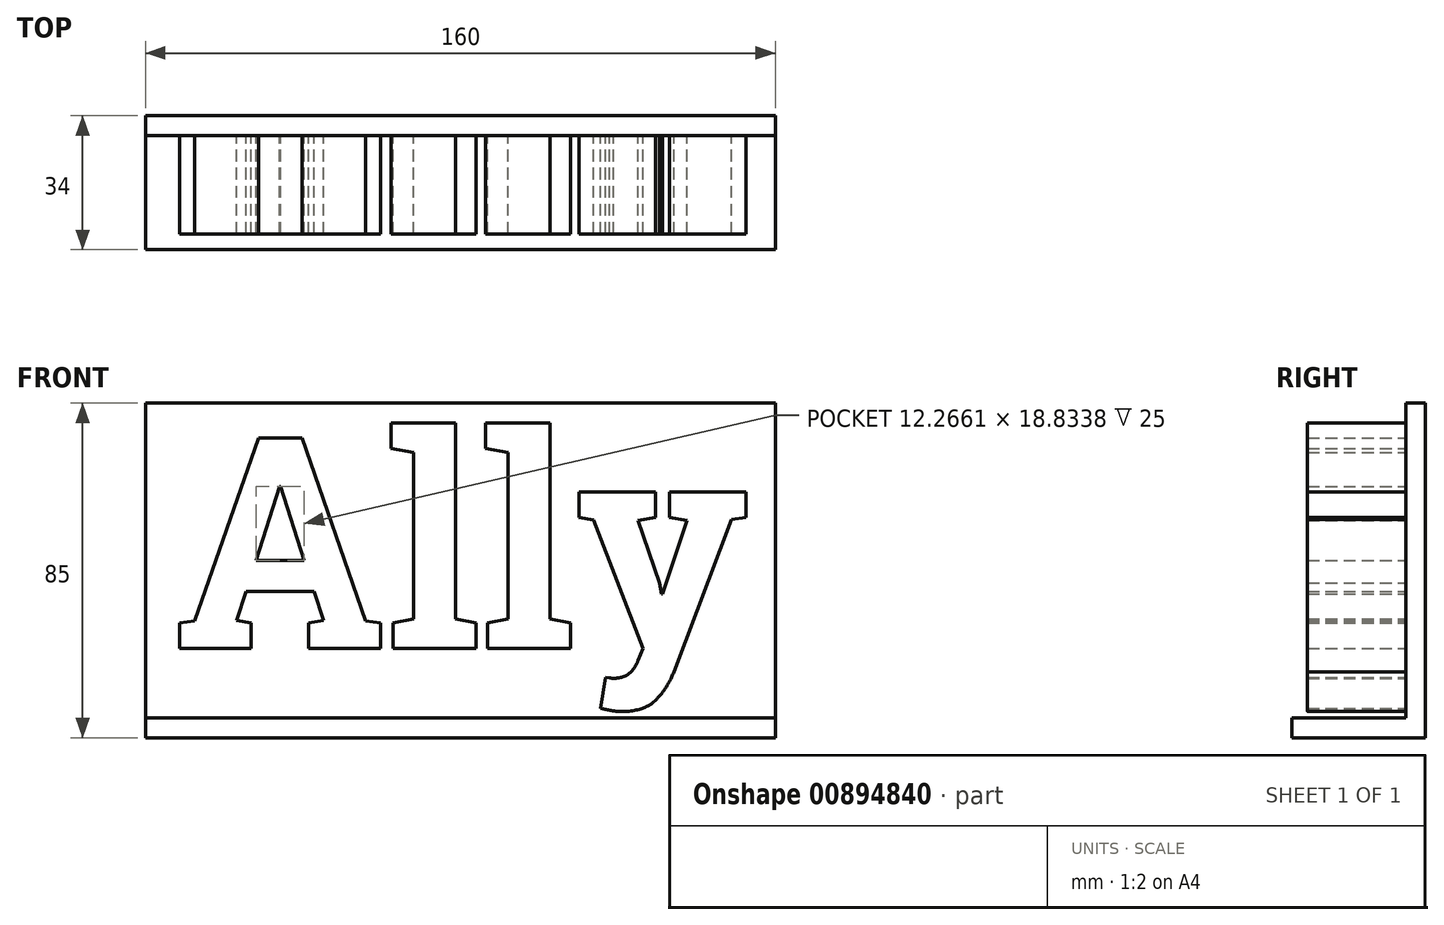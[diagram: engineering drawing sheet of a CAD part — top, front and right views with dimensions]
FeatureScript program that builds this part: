
annotation { "Feature Type Name" : "Feature", "Feature Type Description" : "" }
export const myFeature = defineFeature(function(context is Context, id is Id, definition is map)
    precondition{}
    {
        {
            var Q0;
            Q0=qCreatedBy(makeId("Front.planeOp"),FACE);
            var sketch = newSketch(context, id + "F0", { "sketchPlane" : qUnion([Q0])});
            skText(sketch, "E0", { "text": "Ally", "fontName": "RobotoSlab-Bold.ttf"});
            const initialGuessF0  = {"E0": [-0.06363, 0.04586, 1, 0, 0.05414]};
            skSetInitialGuess(sketch, initialGuessF0);
            skSolve(sketch);
        }
        {
            var Q0;
            Q0 = qSketchRegion(id + "F0", true);
            extrude(context, id + "F1", {"entities" : qUnion([Q0]), "depth" : 25 * mm, "offsetDistance" : 25 * mm});
        }
        {
            var Q0;
            Q0=qCreatedBy(makeId("Front.planeOp"),FACE);
            var sketch = newSketch(context, id + "F2", { "sketchPlane" : qUnion([Q0])});
            skLineSegment(sketch, "E1.bottom", {"start": v(-70.78, 108.16) * mm, "end": v(89.22, 108.16) * mm});
            skLineSegment(sketch, "E1.top", {"start": v(-70.78, 28.16) * mm, "end": v(89.22, 28.16) * mm});
            skLineSegment(sketch, "E1.left", {"start": v(-70.78, 108.16) * mm, "end": v(-70.78, 28.16) * mm});
            skLineSegment(sketch, "E1.right", {"start": v(89.22, 108.16) * mm, "end": v(89.22, 28.16) * mm});
            skSolve(sketch);
        }
        {
            var Q0;
            Q0=makeQuery(id+"F2.imprint","IMPRINT",FACE,{"disambiguationData":[TD([[makeQuery(id+"F2.imprint","IMPRINT",EDGE,{"derivedFrom":sQuery(id+"F2.wireOp",EDGE,"E1.bottom")}),-1.0]])]});
            extrude(context, id + "F3", {"entities" : qUnion([Q0]), "operationType" : NewBodyOperationType.ADD, "oppositeDirection" : true, "depth" : 5 * mm, "offsetDistance" : 25 * mm});
        }
        {
            var Q0;
            Q0=makeQuery(id+"F3.opExtrude","CAP_FACE",FACE,{"disambiguationData":[OSD([sQuery(id+"F2.wireOp",EDGE,"E1.bottom"),sQuery(id+"F2.wireOp",EDGE,"E1.top"),sQuery(id+"F2.wireOp",EDGE,"E1.left"),sQuery(id+"F2.wireOp",EDGE,"E1.right")])],"isStart":true});
            var sketch = newSketch(context, id + "F4", { "sketchPlane" : qUnion([Q0])});
            skLineSegment(sketch, "E2.bottom", {"start": v(89.22, 28.16) * mm, "end": v(-70.78, 28.16) * mm});
            skLineSegment(sketch, "E2.top", {"start": v(89.22, 23.16) * mm, "end": v(-70.78, 23.16) * mm});
            skLineSegment(sketch, "E2.left", {"start": v(89.22, 28.16) * mm, "end": v(89.22, 23.16) * mm});
            skLineSegment(sketch, "E2.right", {"start": v(-70.78, 28.16) * mm, "end": v(-70.78, 23.16) * mm});
            skSolve(sketch);
        }
        {
            var Q0;
            Q0=makeQuery(id+"F4.imprint","IMPRINT",FACE,{"disambiguationData":[TD([[makeQuery(id+"F4.imprint","IMPRINT",EDGE,{"derivedFrom":sQuery(id+"F4.wireOp",EDGE,"E2.bottom")}),-1.0]])]});
            extrude(context, id + "F5", {"entities" : qUnion([Q0]), "operationType" : NewBodyOperationType.ADD, "depth" : 29 * mm, "offsetDistance" : 25 * mm, "hasSecondDirection" : true, "secondDirectionOppositeDirection" : true, "secondDirectionDepth" : 5 * mm});
        }
    });
